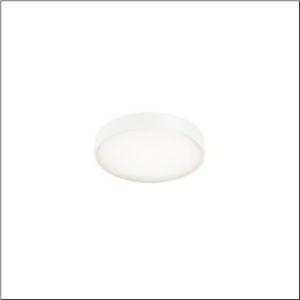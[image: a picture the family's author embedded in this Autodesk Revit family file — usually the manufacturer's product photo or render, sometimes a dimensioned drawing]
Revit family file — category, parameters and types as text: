
# Revit family: round_21_s_51mr34gd0421w
name_source: partatom
category: Lighting Fixtures
units: mm (PartAtom-declared; Revit-internal decimal feet)

## family parameters
Cut with Voids When Loaded = No
Host = Face
Light Source = No
Part Type = Normal
Room Calculation Point = No
Round Connector Dimension = Use Diameter
Shared = No

## types (1)
- Round 21 S (1 x LED, 4090 lm, 28.3 W, 4000K)
    Apparent Load = 28 VA
    CIE Flux Codes = 49 80 96 79 100
    Color Rendering = 80
    Color Temperature = 4000K
    Default Elevation = 1800 mm
    Description = Round 21 S, wall and ceiling luminaire, primary optical cover: cover, of PMMA, opal, light emission: direct/indirect distribution, primary light characteristic: symmetric, installation type: suspended mounting, surface-mounted, LED, rated luminous flux: 4.090lm, luminous efficacy: 135lm/W, light colour: 840, colour temperature: 4000K, control gear: DALI 2, with terminal, 5-pole, mains connection: 230V, AC, 50/60Hz, rated input power: 28.3W, housing, of aluminium, coated, white, diameter: 400mm, height: 62mm, protection rating (complete): IP40, insulation class (complete): insulation class I (protective earthing), certification: CE, impact resistance: IK04, permissible operating ambient temperature: -10..+35°C, packaging unit: 1 piece
    Height = 87 mm
    Lamp = 1 x LED
    Lamp Light Flux = 4090 lm
    Lamp Power = 28.3 W
    Lamp count = 1
    Length = 400 mm
    Luminous efficacy = 145 lm/W
    Manufacturer = Siteco
    ModVariant = No
    Model = 51MR34GD0421W
    Mounting Place = Ceiling
    Mounting Type = Surface mounted
    Number of Poles = 1
    OnlyDefault = Yes
    Power Factor = 1
    Product Name = Round 21 S
    Product group = wall and ceiling luminaire
    ProductGroupID = 304
    Protection Class = Protection class I
    Protection Degree = IP 40
    RLX_Detail_Level = 1
    RLX_Emergency_Light_Flux = 0 lm
    RLX_Emergency_Type = 0
    RLX_Emergency_Type_DB = No
    RlxData = <blob elided: 9921 chars, md5=a384fe93>
    Socket = socket
    Standby Power = 0 W
    System Light Flux = 4090 lm
    System Power = 28 W
    Type Comments = Product without accessories
    Type Image = l_1258307.jpg
    URL = http://relux.com
    VarID = ---
    Voltage = 0 V
    Weight = 0.00 kg
    Width = 0 mm  [stored 0 ft]

note: [stored X ft] marks values corroborated as IEEE doubles in the binary element streams (Revit-internal decimal feet)

## geometry (parser evidence)
native form markers: Sweep x11
no freeform markers — native parametric forms only
